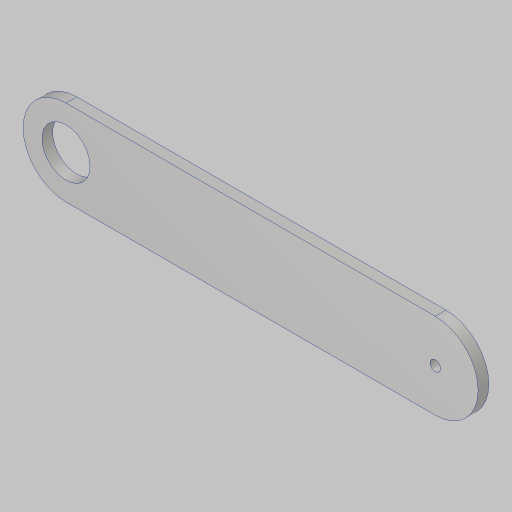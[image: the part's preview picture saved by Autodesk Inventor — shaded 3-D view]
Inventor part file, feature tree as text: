
AUTODESK INVENTOR PART (.ipt)
format: ipt  version: 2023.5 (Build 275446000, 446)  size: 102,400 bytes
history: native  units: in
note: dims shown in document units (in); Inventor stores cm internally (conversion verified against a paired STEP export)
features: extrude x1, sketch x1
ambient origin geometry x8: Origin, YZ Plane, XZ Plane, XY Plane, X Axis, Y Axis, Z Axis, Center Point
bodies: Solid1 (feature_tree)
feature tree (2):
  extrude  "Extrusion1"  Depth=8.621in
  sketch  "Sketch1"  dims[d0=1.125in d1=8.621in d2=2.0in d3=0.25in d4=0.25in d5=0.0in]
